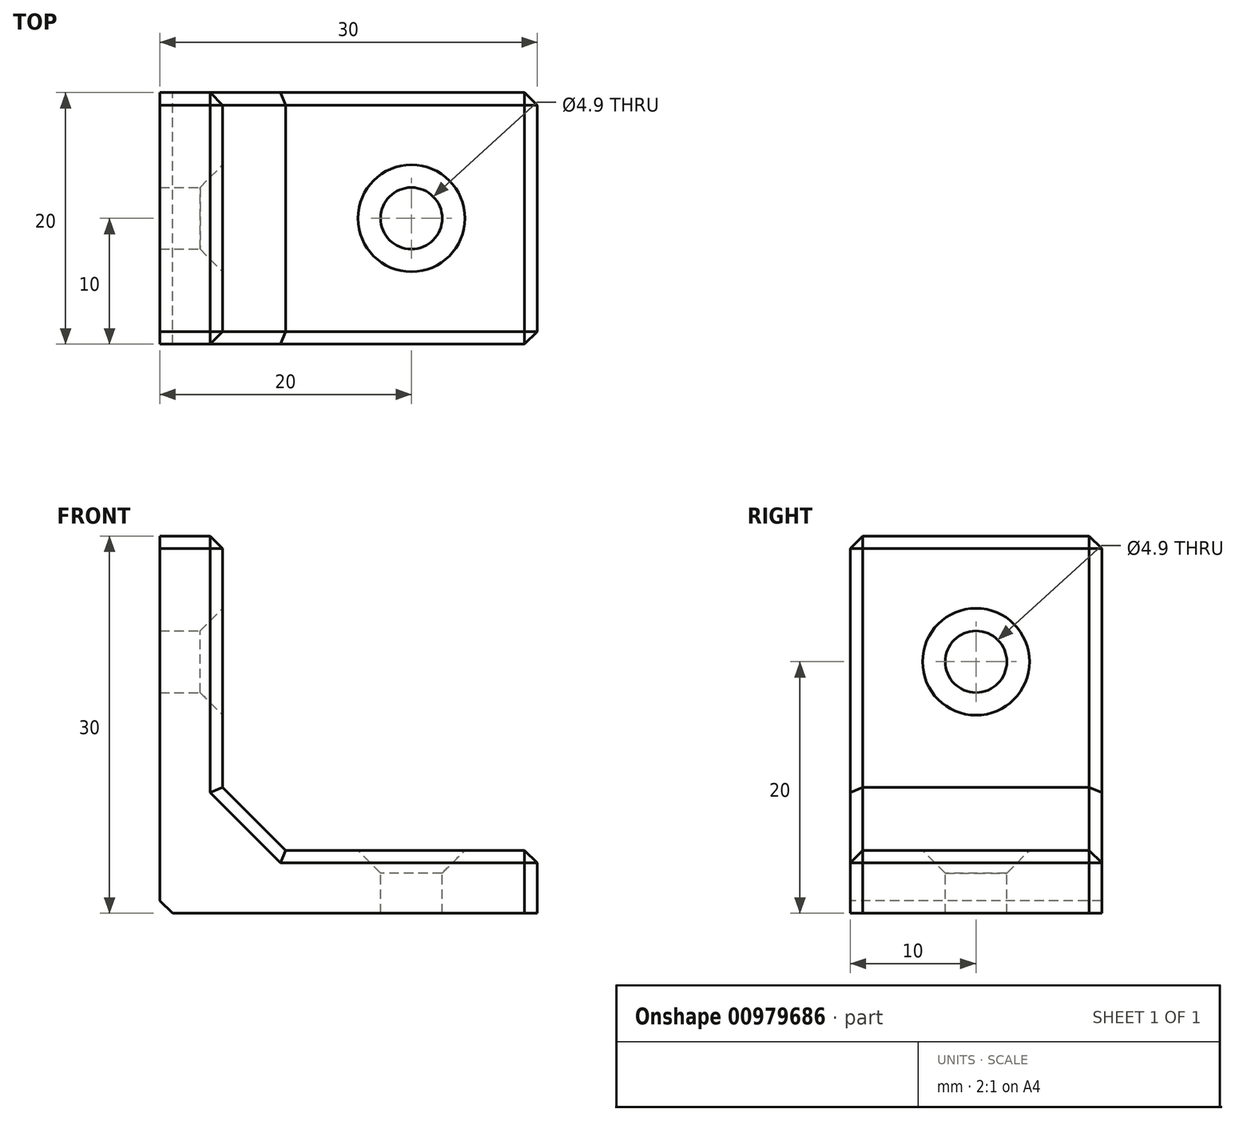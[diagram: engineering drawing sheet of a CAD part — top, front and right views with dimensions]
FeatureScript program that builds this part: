
annotation { "Feature Type Name" : "Feature", "Feature Type Description" : "" }
export const myFeature = defineFeature(function(context is Context, id is Id, definition is map)
    precondition{}
    {
        {
            assignVariable(context, id + "F0", {"name" : "Breite", "anyValue" : 20 * mm});
        }
        {
            var Q0;
            Q0=qCreatedBy(makeId("Front.planeOp"),FACE);
            var sketch = newSketch(context, id + "F1", { "sketchPlane" : qUnion([Q0])});
            skLineSegment(sketch, "E0", {"start": v(0, 0) * mm, "end": v(0, 30) * mm});
            skLineSegment(sketch, "E1", {"start": v(0, 30) * mm, "end": v(5, 30) * mm});
            skLineSegment(sketch, "E2", {"start": v(5, 30) * mm, "end": v(5, 5) * mm});
            skLineSegment(sketch, "E3", {"start": v(5, 5) * mm, "end": v(30, 5) * mm});
            skLineSegment(sketch, "E4", {"start": v(30, 5) * mm, "end": v(30, 0) * mm});
            skLineSegment(sketch, "E5", {"start": v(30, 0) * mm, "end": v(0, 0) * mm});
            skSolve(sketch);
        }
        {
            var Q0;
            Q0=makeQuery(id+"F1.imprint","IMPRINT",FACE,{"disambiguationData":[TD([[makeQuery(id+"F1.imprint","IMPRINT",EDGE,{"derivedFrom":sQuery(id+"F1.wireOp",EDGE,"E0")}),-1.0]])]});
            extrude(context, id + "F2", {"entities" : qUnion([Q0]), "depth" : getVariable(context, 'Breite'), "offsetDistance" : 25 * mm});
        }
        {
            var Q0;
            Q0=makeQuery(id+"F2.opExtrude","SWEPT_EDGE",EDGE,{"disambiguationData":[OSD([sQuery(id+"F1.wireOp",EDGE,"E2"),sQuery(id+"F1.wireOp",EDGE,"E3")])]});
            chamfer(context, id + "F3", {"entities" : qUnion([Q0]), "width" : 5 * mm, "tangentPropagation" : true});
        }
        {
            var Q0;
            Q0=makeQuery(id+"F2.opExtrude","SWEPT_FACE",FACE,{"disambiguationData":[OSD([sQuery(id+"F1.wireOp",EDGE,"E3")])]});
            var sketch = newSketch(context, id + "F4", { "sketchPlane" : qUnion([Q0])});
            skLineSegment(sketch, "E6", {"start": v(30, -10) * mm, "end": v(10, -10) * mm, "construction": true});
            skLineSegment(sketch, "E7", {"start": v(10, -10) * mm, "end": v(30, -20) * mm, "construction": true});
            skLineSegment(sketch, "E8", {"start": v(10, -10) * mm, "end": v(30, 0) * mm, "construction": true});
            skPoint(sketch, "E9", {"position": v(20, -15) * mm});
            skPoint(sketch, "E10", {"position": v(20, -5) * mm});
            skPoint(sketch, "E11", {"position": v(20, -10) * mm});
            skSolve(sketch);
        }
        {
            var Q0;
            Q0=makeQuery(id+"F2.opExtrude","SWEPT_FACE",FACE,{"disambiguationData":[OSD([sQuery(id+"F1.wireOp",EDGE,"E2")])]});
            var sketch = newSketch(context, id + "F5", { "sketchPlane" : qUnion([Q0])});
            skLineSegment(sketch, "E12", {"start": v(-10, 10) * mm, "end": v(-10, 30) * mm, "construction": true});
            skLineSegment(sketch, "E13", {"start": v(-10, 30) * mm, "end": v(-20, 10) * mm, "construction": true});
            skLineSegment(sketch, "E14", {"start": v(-10, 30) * mm, "end": v(0, 10) * mm, "construction": true});
            skPoint(sketch, "E15", {"position": v(-15, 20) * mm});
            skPoint(sketch, "E16", {"position": v(-5, 20) * mm});
            skPoint(sketch, "E17", {"position": v(-10, 20) * mm});
            skSolve(sketch);
        }
        {
            var Q0;
            Q0=sQuery(id+"F5.wireOp",VERTEX,"E17");
            var Q1;
            Q1=sQuery(id+"F4.wireOp",VERTEX,"E11");
            var Q2;
            Q2=makeQuery(id+"F2.opExtrude","SWEPT_BODY",BODY,{"disambiguationData":[OSD([sQuery(id+"F1.wireOp",EDGE,"E0"),sQuery(id+"F1.wireOp",EDGE,"E1"),sQuery(id+"F1.wireOp",EDGE,"E2"),sQuery(id+"F1.wireOp",EDGE,"E3"),sQuery(id+"F1.wireOp",EDGE,"E4"),sQuery(id+"F1.wireOp",EDGE,"E5")])]});
            hole(context, id + "F6", {"style" : HoleStyle.C_SINK, "endStyle" : HoleEndStyle.BLIND, "holeDiameter" : 4.9 * mm, "cSinkDiameter" : 8.5 * mm, "cSinkAngle" : 90 * degree, "majorDiameter" : 4.5 * mm, "holeDepth" : 16 * mm, "isTappedThrough" : true, "tappedDepth" : 12 * mm, "tapClearance" : 3, "locations" : qUnion([Q0, Q1]), "scope" : qUnion([Q2])});
        }
        {
            var Q0;
            Q0=makeQuery(id+"F2.opExtrude","SWEPT_EDGE",EDGE,{"disambiguationData":[OSD([sQuery(id+"F1.wireOp",EDGE,"E3"),sQuery(id+"F1.wireOp",EDGE,"E4")])]});
            var Q1;
            Q1=makeQuery(id+"F2.opExtrude","SWEPT_EDGE",EDGE,{"disambiguationData":[OSD([sQuery(id+"F1.wireOp",EDGE,"E1"),sQuery(id+"F1.wireOp",EDGE,"E2")])]});
            var Q2;
            Q2=makeQuery(id+"F2.opExtrude","CAP_EDGE",EDGE,{"disambiguationData":[OSD([sQuery(id+"F1.wireOp",EDGE,"E4")])],"isStart":false});
            var Q3;
            Q3=makeQuery(id+"F2.opExtrude","CAP_EDGE",EDGE,{"disambiguationData":[OSD([sQuery(id+"F1.wireOp",EDGE,"E3")])],"isStart":false});
            var Q4;
            {var subQ0=sQuery(id+"F1.wireOp",EDGE,"E3");var subQ1=sQuery(id+"F1.wireOp",EDGE,"E2");Q4=makeQuery(id+"F3.opChamfer","BLEND_EDGE",EDGE,{"blendedFrom":[makeQuery(id+"F2.opExtrude","SWEPT_EDGE",EDGE,{"disambiguationData":[OSD([subQ1,subQ0])]}),makeQuery(id+"F2.opExtrude","CAP_FACE",FACE,{"disambiguationData":[OSD([sQuery(id+"F1.wireOp",EDGE,"E0"),sQuery(id+"F1.wireOp",EDGE,"E1"),subQ1,subQ0,sQuery(id+"F1.wireOp",EDGE,"E4"),sQuery(id+"F1.wireOp",EDGE,"E5")])],"isStart":false})],"blendedInto":[makeQuery(id+"F2.opExtrude","CAP_FACE",FACE,{"disambiguationData":[OSD([sQuery(id+"F1.wireOp",EDGE,"E0"),sQuery(id+"F1.wireOp",EDGE,"E1"),subQ1,subQ0,sQuery(id+"F1.wireOp",EDGE,"E4"),sQuery(id+"F1.wireOp",EDGE,"E5")])],"isStart":false})]});}
            var Q5;
            Q5=makeQuery(id+"F2.opExtrude","CAP_EDGE",EDGE,{"disambiguationData":[OSD([sQuery(id+"F1.wireOp",EDGE,"E1")])],"isStart":false});
            var Q6;
            Q6=makeQuery(id+"F2.opExtrude","CAP_EDGE",EDGE,{"disambiguationData":[OSD([sQuery(id+"F1.wireOp",EDGE,"E4")])],"isStart":true});
            var Q7;
            Q7=makeQuery(id+"F2.opExtrude","CAP_EDGE",EDGE,{"disambiguationData":[OSD([sQuery(id+"F1.wireOp",EDGE,"E3")])],"isStart":true});
            var Q8;
            {var subQ0=sQuery(id+"F1.wireOp",EDGE,"E3");var subQ1=sQuery(id+"F1.wireOp",EDGE,"E2");Q8=makeQuery(id+"F3.opChamfer","BLEND_EDGE",EDGE,{"blendedFrom":[makeQuery(id+"F2.opExtrude","SWEPT_EDGE",EDGE,{"disambiguationData":[OSD([subQ1,subQ0])]}),makeQuery(id+"F2.opExtrude","CAP_FACE",FACE,{"disambiguationData":[OSD([sQuery(id+"F1.wireOp",EDGE,"E0"),sQuery(id+"F1.wireOp",EDGE,"E1"),subQ1,subQ0,sQuery(id+"F1.wireOp",EDGE,"E4"),sQuery(id+"F1.wireOp",EDGE,"E5")])],"isStart":true})],"blendedInto":[makeQuery(id+"F2.opExtrude","CAP_FACE",FACE,{"disambiguationData":[OSD([sQuery(id+"F1.wireOp",EDGE,"E0"),sQuery(id+"F1.wireOp",EDGE,"E1"),subQ1,subQ0,sQuery(id+"F1.wireOp",EDGE,"E4"),sQuery(id+"F1.wireOp",EDGE,"E5")])],"isStart":true})]});}
            var Q9;
            Q9=makeQuery(id+"F2.opExtrude","CAP_EDGE",EDGE,{"disambiguationData":[OSD([sQuery(id+"F1.wireOp",EDGE,"E1")])],"isStart":true});
            var Q10;
            Q10=makeQuery(id+"F2.opExtrude","CAP_EDGE",EDGE,{"disambiguationData":[OSD([sQuery(id+"F1.wireOp",EDGE,"E2")])],"isStart":false});
            var Q11;
            Q11=makeQuery(id+"F2.opExtrude","CAP_EDGE",EDGE,{"disambiguationData":[OSD([sQuery(id+"F1.wireOp",EDGE,"E2")])],"isStart":true});
            chamfer(context, id + "F7", {"entities" : qUnion([Q0, Q1, Q2, Q3, Q4, Q5, Q6, Q7, Q8, Q9, Q10, Q11]), "width" : 1 * mm, "tangentPropagation" : true});
        }
        {
            var Q0;
            Q0=makeQuery(id+"F2.opExtrude","SWEPT_EDGE",EDGE,{"disambiguationData":[OSD([sQuery(id+"F1.wireOp",EDGE,"E0"),sQuery(id+"F1.wireOp",EDGE,"E5")])]});
            chamfer(context, id + "F8", {"entities" : qUnion([Q0]), "width" : 1 * mm, "tangentPropagation" : true});
        }
    });
